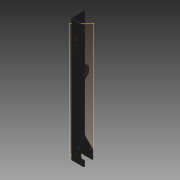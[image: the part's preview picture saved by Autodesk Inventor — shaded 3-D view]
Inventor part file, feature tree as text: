
AUTODESK INVENTOR PART (.ipt)
format: ipt  version: 2015 (Build 190159000, 159)  size: 411,136 bytes
history: native  units: mm
features: extrude x10, hole x8, fillet x6, other x3, plane x1, mirror x1, chamfer x1
ambient origin geometry x8: Origin, YZ Plane, XZ Plane, XY Plane, X Axis, Y Axis, Z Axis, Center Point
bodies: Solid1 (feature_tree)
feature tree (30):
  extrude  "Extrusión1"  Depth=50.0mm
  plane  "Plano de trabajo1"
  fillet  "Empalme1"  Radius=50.0mm
  extrude  "Extrusión2"  Depth=2.0mm
  extrude  "Extrusión3"  Depth=440.0mm TaperAngle=0.0deg
  hole  "Agujero2"  [1 undecoded]
  mirror  "Simetría3"
  extrude  "Extrusión4"  Depth=25.0mm
  extrude  "Extrusión5"  Depth=4.0mm TaperAngle=45.0deg
  fillet  "Empalme2"  Radius=51.0mm
  hole  "Agujero4"  [1 undecoded]
  extrude  "Extrusión6"  Depth=13.0mm
  hole  "Agujero5"  [1 undecoded]
  hole  "Agujero6"  [1 undecoded]
  extrude  "Extrusión7"  Depth=4.0mm
  chamfer  "Chaflán1"  Distance=8.0mm
  fillet  "Empalme3"  Radius=10.0mm
  hole  "Agujero7"  [1 undecoded]
  extrude  "Extrusión8"  Depth=10.0mm TaperAngle=0.0deg
  fillet  "Redondeo de esquina1"  [1 undecoded]
  hole  "Agujero9"  [1 undecoded]
  hole  "Agujero10"  [1 undecoded]
  other  "Desplazar cara1"
  other  "Desplazar cara2"
  hole  "Agujero11"  [1 undecoded]
  fillet  "Redondeo de esquina2"  Radius=2.0mm
  extrude  "Extrusión9"  Depth=12.0mm
  extrude  "Extrusión10"  Depth=3.0mm
  fillet  "Redondeo de esquina3"  Radius=15.0mm
  other  "Definición1"
note: 9 required parameter values undecoded (feature->parameter linkage not recoverable at this tier; creation-order binding heuristic only, values carry confidence <= 0.55)
